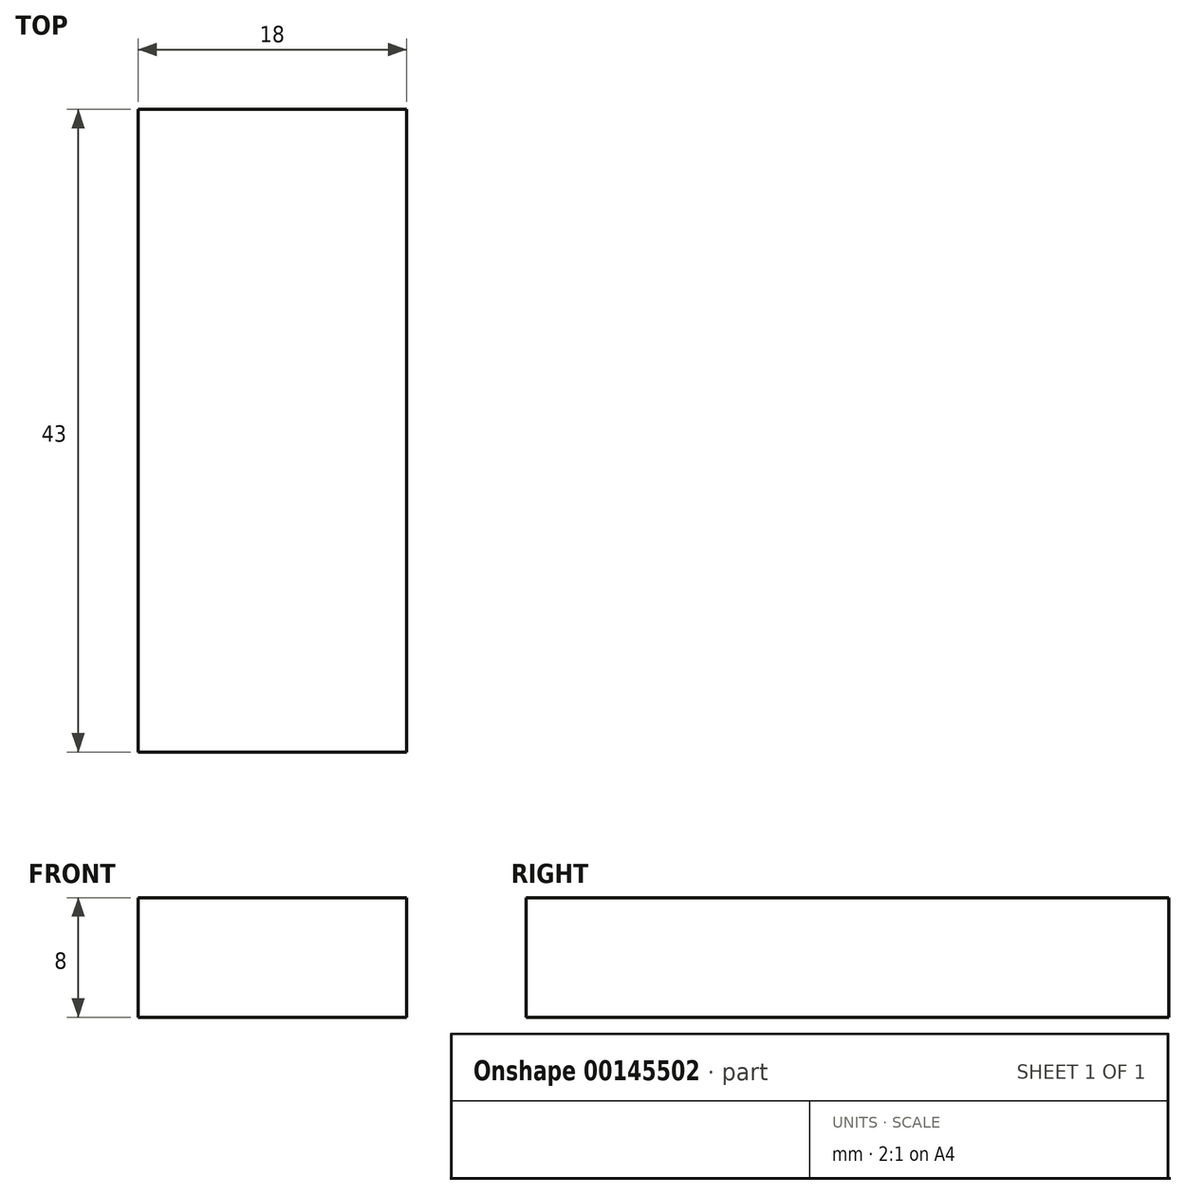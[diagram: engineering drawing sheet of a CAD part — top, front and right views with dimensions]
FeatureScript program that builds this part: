
annotation { "Feature Type Name" : "Feature", "Feature Type Description" : "" }
export const myFeature = defineFeature(function(context is Context, id is Id, definition is map)
    precondition{}
    {
        {
            var Q0;
            Q0=qCreatedBy(makeId("Front.planeOp"),FACE);
            var sketch = newSketch(context, id + "F0", { "sketchPlane" : qUnion([Q0])});
            skLineSegment(sketch, "E0.bottom", {"start": v(-9, 0) * mm, "end": v(9, 0) * mm});
            skLineSegment(sketch, "E0.top", {"start": v(-9, -8) * mm, "end": v(9, -8) * mm});
            skLineSegment(sketch, "E0.left", {"start": v(-9, 0) * mm, "end": v(-9, -8) * mm});
            skLineSegment(sketch, "E0.right", {"start": v(9, 0) * mm, "end": v(9, -8) * mm});
            skSolve(sketch);
        }
        {
            var Q0;
            Q0 = qSketchRegion(id + "F0", true);
            extrude(context, id + "F1", {"entities" : qUnion([Q0]), "depth" : 43 * mm});
        }
    });
